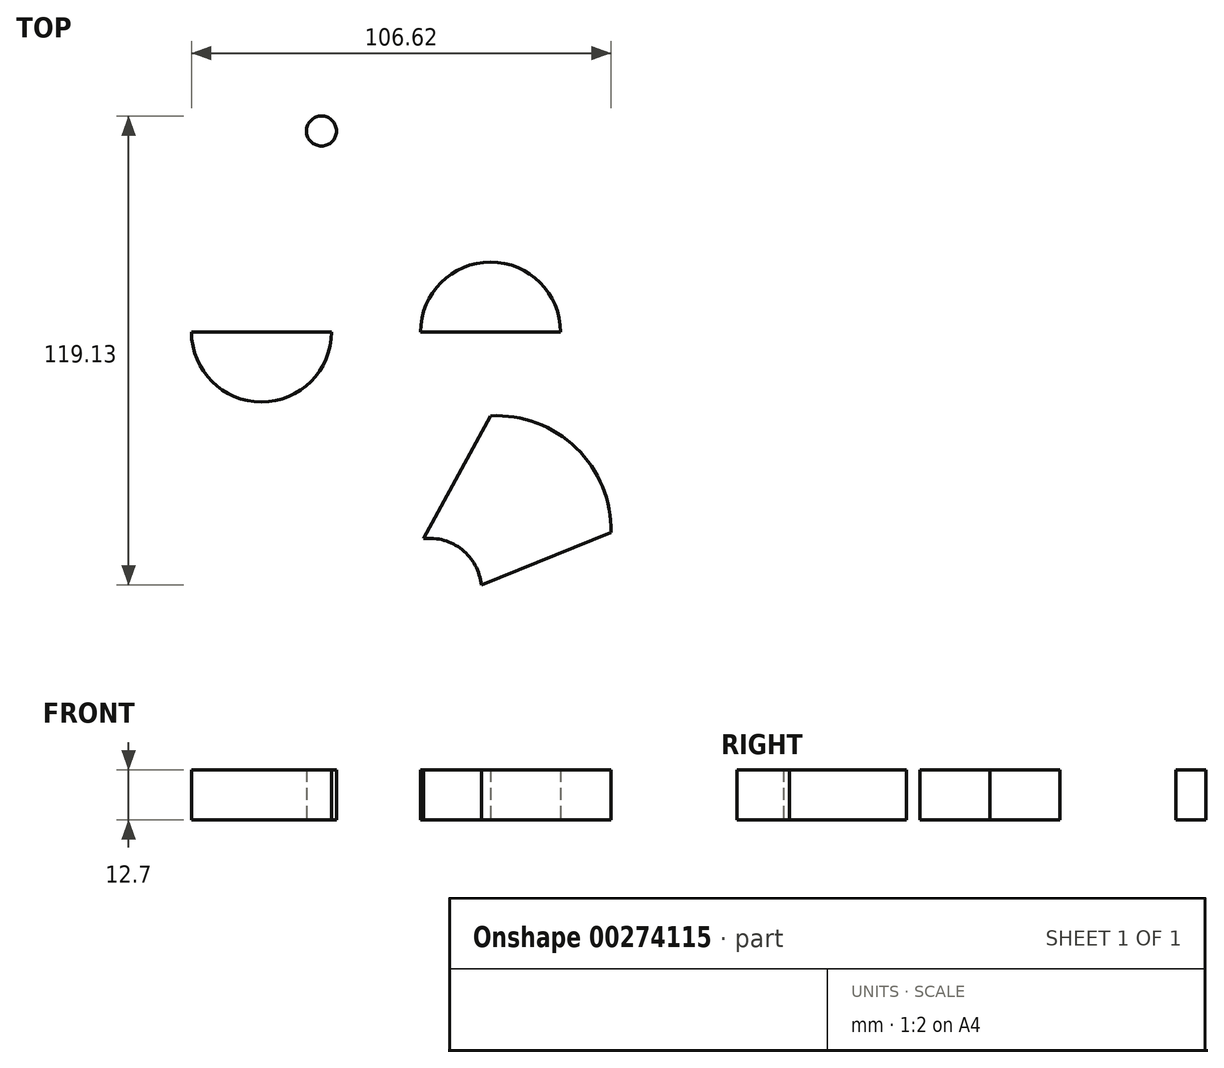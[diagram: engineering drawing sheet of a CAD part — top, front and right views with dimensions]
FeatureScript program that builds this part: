
annotation { "Feature Type Name" : "Feature", "Feature Type Description" : "" }
export const myFeature = defineFeature(function(context is Context, id is Id, definition is map)
    precondition{}
    {
        {
            var Q0;
            Q0=qCreatedBy(makeId("Top.planeOp"),FACE);
            var sketch = newSketch(context, id + "F0", { "sketchPlane" : qUnion([Q0])});
            skArc(sketch, "E0", {"start": v(-17.78, 0) * mm, "mid": v(0, 17.78) * mm, "end": v(17.78, 0) * mm});
            skLineSegment(sketch, "E1", {"start": v(-17.78, 0) * mm, "end": v(17.78, 0) * mm});
            skArc(sketch, "E2", {"start": v(-40.43, 0) * mm, "mid": v(-58.2, -17.78) * mm, "end": v(-75.99, 0) * mm});
            skLineSegment(sketch, "E3", {"start": v(-75.99, 0) * mm, "end": v(-40.43, 0) * mm});
            skLineSegment(sketch, "E4", {"start": v(0, -21.3) * mm, "end": v(-17.05, -52.51) * mm});
            skArc(sketch, "E5", {"start": v(-17.05, -52.51) * mm, "mid": v(-7.24, -55.3) * mm, "end": v(-2.35, -64.25) * mm});
            skLineSegment(sketch, "E6", {"start": v(-2.35, -64.25) * mm, "end": v(30.63, -50.94) * mm});
            skArc(sketch, "E7", {"start": v(30.63, -50.94) * mm, "mid": v(21.75, -29.47) * mm, "end": v(0, -21.3) * mm});
            skCircle(sketch, "E8", {"center": v(-42.95, 51.07) * mm, "radius": 3.81 * mm});
            skLineSegment(sketch, "E9", {"start": v(14.14, -57.6) * mm, "end": v(-8.52, -36.9) * mm});
            skSolve(sketch);
        }
        {
            var Q0;
            Q0 = qSketchRegion(id + "F0", true);
            extrude(context, id + "F1", {"entities" : qUnion([Q0]), "depth" : 12.7 * mm});
        }
    });
